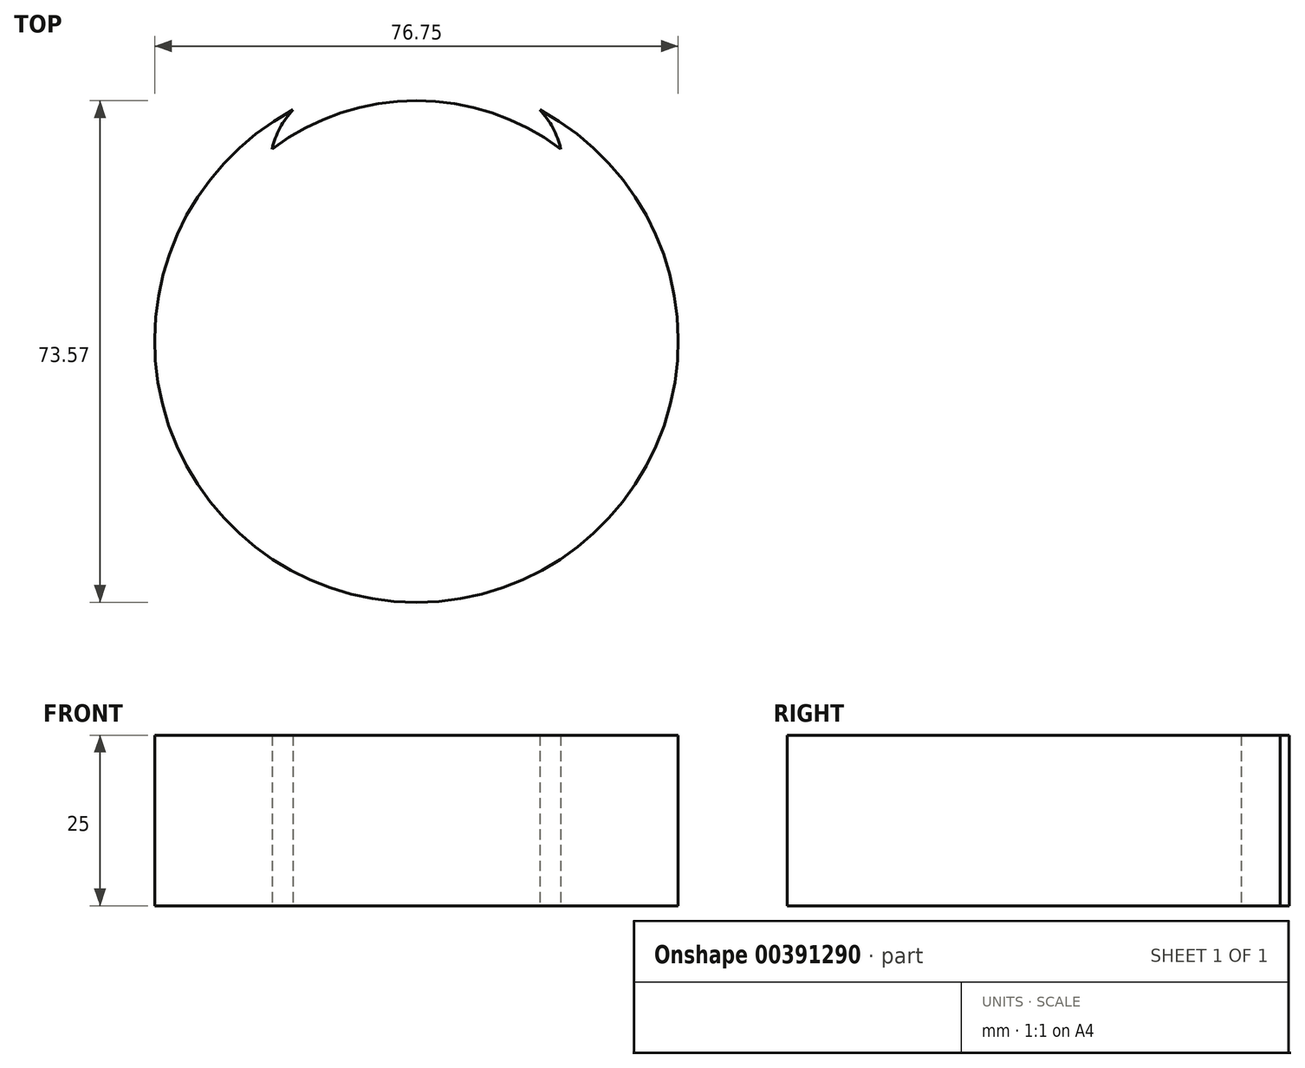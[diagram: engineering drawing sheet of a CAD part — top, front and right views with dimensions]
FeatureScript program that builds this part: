
annotation { "Feature Type Name" : "Feature", "Feature Type Description" : "" }
export const myFeature = defineFeature(function(context is Context, id is Id, definition is map)
    precondition{}
    {
        {
            var Q0;
            Q0=qCreatedBy(makeId("Top.planeOp"),FACE);
            var sketch = newSketch(context, id + "F0", { "sketchPlane" : qUnion([Q0])});
            skCircle(sketch, "E0", {"center": v(0, 0) * mm, "radius": 35.2 * mm, "construction": true});
            skLineSegment(sketch, "E1", {"start": v(-21.16, 28.13) * mm, "end": v(21.16, 28.13) * mm, "construction": true});
            skCircle(sketch, "E2", {"center": v(0, 0) * mm, "radius": 38.38 * mm});
            skArc(sketch, "E3", {"start": v(-21.16, 28.13) * mm, "mid": v(0, 35.2) * mm, "end": v(21.16, 28.13) * mm});
            skLineSegment(sketch, "E4", {"start": v(0, 0) * mm, "end": v(-21.16, 28.13) * mm, "construction": true});
            skLineSegment(sketch, "E5", {"start": v(-21.16, 28.13) * mm, "end": v(-29.76, 39.57) * mm, "construction": true});
            skLineSegment(sketch, "E6", {"start": v(0, 0) * mm, "end": v(21.16, 28.13) * mm, "construction": true});
            skLineSegment(sketch, "E7", {"start": v(21.16, 28.13) * mm, "end": v(30.36, 40.37) * mm, "construction": true});
            skLineSegment(sketch, "E8", {"start": v(30.36, 40.37) * mm, "end": v(27.73, 36.88) * mm});
            skLineSegment(sketch, "E9", {"start": v(-21.16, 28.13) * mm, "end": v(-18.07, 33.85) * mm, "construction": true});
            skPoint(sketch, "E9.endSnap0", {"position": v(-25.46, 33.85) * mm});
            skArc(sketch, "E10", {"start": v(-18.07, 33.85) * mm, "mid": v(-20, 31.2) * mm, "end": v(-21.16, 28.13) * mm});
            skLineSegment(sketch, "E11", {"start": v(21.16, 28.13) * mm, "end": v(18.07, 33.85) * mm, "construction": true});
            skArc(sketch, "E12", {"start": v(21.16, 28.13) * mm, "mid": v(20, 31.2) * mm, "end": v(18.07, 33.85) * mm});
            skSolve(sketch);
        }
        {
            var Q0;
            Q0=makeQuery(id+"F0.imprint","IMPRINT",FACE,{"disambiguationData":[TD([[makeQuery(id+"F0.imprint","IMPRINT",EDGE,{"derivedFrom":sQuery(id+"F0.wireOp",EDGE,"E3")}),1.0]])]});
            extrude(context, id + "F1", {"entities" : qUnion([Q0]), "depth" : 25 * mm});
        }
    });
